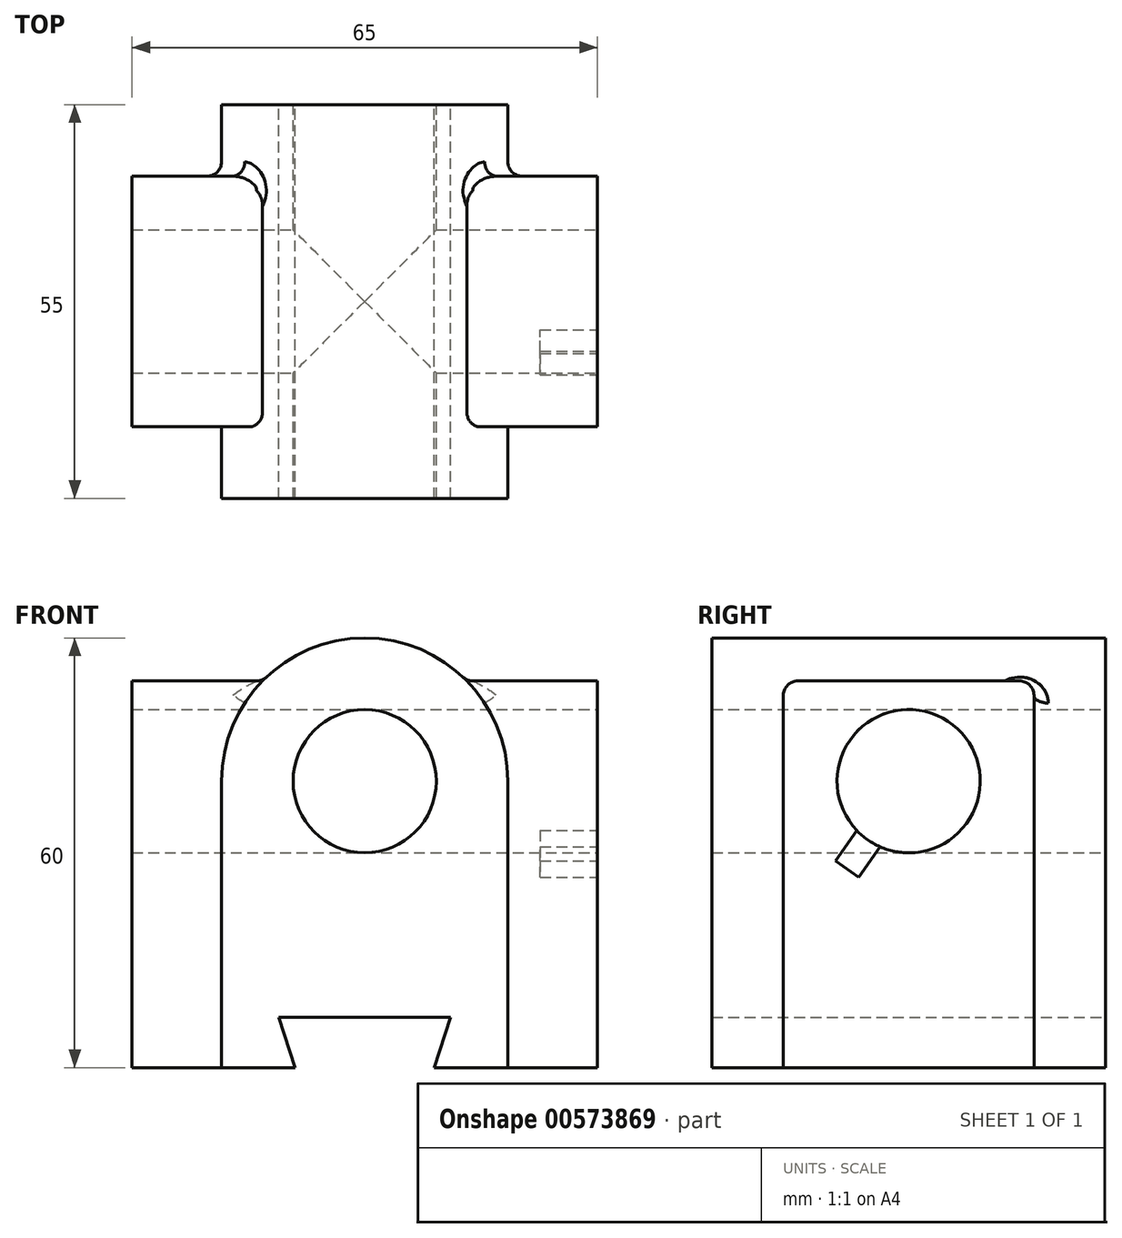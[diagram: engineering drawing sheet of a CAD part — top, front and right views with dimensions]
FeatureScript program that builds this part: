
annotation { "Feature Type Name" : "Feature", "Feature Type Description" : "" }
export const myFeature = defineFeature(function(context is Context, id is Id, definition is map)
    precondition{}
    {
        {
            var Q0;
            Q0=qCreatedBy(makeId("Front.planeOp"),FACE);
            var sketch = newSketch(context, id + "F0", { "sketchPlane" : qUnion([Q0])});
            skLineSegment(sketch, "E0.top", {"start": v(-20, -40) * mm, "end": v(-9.73, -40) * mm});
            skLineSegment(sketch, "E0.left", {"start": v(-20, 0) * mm, "end": v(-20, -40) * mm});
            skLineSegment(sketch, "E0.right", {"start": v(20, 0) * mm, "end": v(20, -40) * mm});
            skArc(sketch, "E1", {"start": v(20, 0) * mm, "mid": v(0, 20) * mm, "end": v(-20, 0) * mm});
            skCircle(sketch, "E2", {"center": v(0, 0) * mm, "radius": 10 * mm});
            skLineSegment(sketch, "E3", {"start": v(-12, -33) * mm, "end": v(-9.73, -40) * mm});
            skLineSegment(sketch, "E4", {"start": v(9.73, -40) * mm, "end": v(12, -33) * mm});
            skLineSegment(sketch, "E5", {"start": v(12, -33) * mm, "end": v(-12, -33) * mm});
            skLineSegment(sketch, "E6.trimOffspring", {"start": v(9.73, -40) * mm, "end": v(20, -40) * mm});
            skSolve(sketch);
        }
        {
            var Q0;
            Q0 = qSketchRegion(id + "F0", true);
            extrude(context, id + "F1", {"entities" : qUnion([Q0]), "depth" : 55 * mm, "offsetDistance" : 25 * mm});
        }
        {
            var Q0;
            Q0=makeQuery(id+"F1.opExtrude","SWEPT_FACE",FACE,{"disambiguationData":[OSD([sQuery(id+"F0.wireOp",EDGE,"E0.left")])]});
            var sketch = newSketch(context, id + "F2", { "sketchPlane" : qUnion([Q0])});
            skLineSegment(sketch, "E7.bottom", {"start": v(10, 14) * mm, "end": v(45, 14) * mm});
            skLineSegment(sketch, "E7.top", {"start": v(10, -40) * mm, "end": v(45, -40) * mm});
            skLineSegment(sketch, "E7.left", {"start": v(10, 14) * mm, "end": v(10, -40) * mm});
            skLineSegment(sketch, "E7.right", {"start": v(45, 14) * mm, "end": v(45, -40) * mm});
            skSolve(sketch);
        }
        {
            var Q0;
            {var subQ0=sQuery(id+"F2.wireOp",EDGE,"E7.bottom");Q0=makeQuery(id+"F2.imprint","IMPRINT",FACE,{"disambiguationData":[TD([[makeQuery(id+"F2.imprint","IMPRINT",EDGE,{"derivedFrom":subQ0}),-1.0]])]});}
            var Q1;
            {var subQ0=sQuery(id+"F2.wireOp",EDGE,"E7.top");Q1=makeQuery(id+"F2.imprint","IMPRINT",FACE,{"disambiguationData":[TD([[makeQuery(id+"F2.imprint","IMPRINT",EDGE,{"derivedFrom":subQ0}),-1.0]])]});}
            extrude(context, id + "F3", {"entities" : qUnion([Q0, Q1]), "operationType" : NewBodyOperationType.ADD, "depth" : 12.5 * mm, "offsetDistance" : 25 * mm});
        }
        {
            var Q0;
            Q0=makeQuery(id+"F1.opExtrude","SWEPT_FACE",FACE,{"disambiguationData":[OSD([sQuery(id+"F0.wireOp",EDGE,"E0.right")])]});
            var sketch = newSketch(context, id + "F4", { "sketchPlane" : qUnion([Q0])});
            skLineSegment(sketch, "E8.bottom", {"start": v(-45, 14) * mm, "end": v(-10, 14) * mm});
            skLineSegment(sketch, "E8.top", {"start": v(-45, -40) * mm, "end": v(-10, -40) * mm});
            skLineSegment(sketch, "E8.left", {"start": v(-45, 14) * mm, "end": v(-45, -40) * mm});
            skLineSegment(sketch, "E8.right", {"start": v(-10, 14) * mm, "end": v(-10, -40) * mm});
            skSolve(sketch);
        }
        {
            var Q0;
            {var subQ0=sQuery(id+"F4.wireOp",EDGE,"E8.top");Q0=makeQuery(id+"F4.imprint","IMPRINT",FACE,{"disambiguationData":[TD([[makeQuery(id+"F4.imprint","IMPRINT",EDGE,{"derivedFrom":subQ0}),1.0]])]});}
            var Q1;
            {var subQ0=sQuery(id+"F4.wireOp",EDGE,"E8.bottom");Q1=makeQuery(id+"F4.imprint","IMPRINT",FACE,{"disambiguationData":[TD([[makeQuery(id+"F4.imprint","IMPRINT",EDGE,{"derivedFrom":subQ0}),-1.0]])]});}
            extrude(context, id + "F5", {"entities" : qUnion([Q0, Q1]), "operationType" : NewBodyOperationType.ADD, "depth" : 12.5 * mm, "offsetDistance" : 25 * mm});
        }
        {
            var Q0;
            Q0=makeQuery(id+"F5.opExtrude","SWEPT_FACE",FACE,{"disambiguationData":[OSD([sQuery(id+"F4.wireOp",EDGE,"E8.left")])]});
            var sketch = newSketch(context, id + "F6", { "sketchPlane" : qUnion([Q0])});
            skLineSegment(sketch, "E9.0", {"start": v(20, 14) * mm, "end": v(20, 0) * mm});
            skLineSegment(sketch, "E10.0", {"start": v(-20, 14) * mm, "end": v(-20, 0) * mm});
            skLineSegment(sketch, "E11", {"start": v(20, 14) * mm, "end": v(14.28, 14) * mm});
            skLineSegment(sketch, "E12", {"start": v(-20, 14) * mm, "end": v(-14.28, 14) * mm});
            skArc(sketch, "E13.0", {"start": v(20, 0) * mm, "mid": v(0, 20) * mm, "end": v(-20, 0) * mm});
            skSolve(sketch);
        }
        {
            var Q0;
            {var subQ0=sQuery(id+"F6.wireOp",EDGE,"E10.0");Q0=makeQuery(id+"F6.imprint","IMPRINT",FACE,{"disambiguationData":[TD([[makeQuery(id+"F6.imprint","IMPRINT",EDGE,{"derivedFrom":subQ0}),1.0]])]});}
            var Q1;
            {var subQ0=sQuery(id+"F6.wireOp",EDGE,"E9.0");Q1=makeQuery(id+"F6.imprint","IMPRINT",FACE,{"disambiguationData":[TD([[makeQuery(id+"F6.imprint","IMPRINT",EDGE,{"derivedFrom":subQ0}),-1.0]])]});}
            extrude(context, id + "F7", {"entities" : qUnion([Q0, Q1]), "operationType" : NewBodyOperationType.ADD, "oppositeDirection" : true, "depth" : 35 * mm, "offsetDistance" : 25 * mm});
        }
        {
            var Q0;
            Q0=makeQuery(id+"F5.opExtrude","CAP_FACE",FACE,{"disambiguationData":[OSD([sQuery(id+"F4.wireOp",EDGE,"E8.bottom"),sQuery(id+"F4.wireOp",EDGE,"E8.top"),sQuery(id+"F4.wireOp",EDGE,"E8.left"),sQuery(id+"F4.wireOp",EDGE,"E8.right")])],"isStart":false});
            var sketch = newSketch(context, id + "F8", { "sketchPlane" : qUnion([Q0])});
            skCircle(sketch, "E14", {"center": v(-27.5, 0) * mm, "radius": 10 * mm});
            skSolve(sketch);
        }
        {
            var Q0;
            Q0=makeQuery(id+"F8.imprint","IMPRINT",FACE,{"disambiguationData":[TD([[makeQuery(id+"F8.imprint","IMPRINT",EDGE,{"derivedFrom":sQuery(id+"F8.wireOp",EDGE,"E14")}),1.0]])]});
            extrude(context, id + "F9", {"entities" : qUnion([Q0]), "operationType" : NewBodyOperationType.REMOVE, "oppositeDirection" : true, "depth" : 70 * mm, "offsetDistance" : 25 * mm});
        }
        {
            var Q0;
            Q0=makeQuery(id+"F7.boolean.opBoolean","MERGE",EDGE,{"derivedFrom":[makeQuery(id+"F3.opExtrude","SWEPT_EDGE",EDGE,{"disambiguationData":[OSD([sQuery(id+"F2.wireOp",EDGE,"E7.bottom"),sQuery(id+"F2.wireOp",EDGE,"E7.left")])]}),makeQuery(id+"F7.opExtrude","CAP_EDGE",EDGE,{"disambiguationData":[OSD([sQuery(id+"F6.wireOp",EDGE,"E12")])],"isStart":false})]});
            var Q1;
            Q1=makeQuery(id+"F7.boolean.opBoolean","MERGE",EDGE,{"derivedFrom":[makeQuery(id+"F3.opExtrude","SWEPT_EDGE",EDGE,{"disambiguationData":[OSD([sQuery(id+"F2.wireOp",EDGE,"E7.bottom"),sQuery(id+"F2.wireOp",EDGE,"E7.right")])]}),makeQuery(id+"F7.opExtrude","CAP_EDGE",EDGE,{"disambiguationData":[OSD([sQuery(id+"F6.wireOp",EDGE,"E12")])],"isStart":true})]});
            var Q2;
            Q2=makeQuery(id+"F7.boolean.opBoolean","MERGE",EDGE,{"derivedFrom":[makeQuery(id+"F5.opExtrude","SWEPT_EDGE",EDGE,{"disambiguationData":[OSD([sQuery(id+"F4.wireOp",EDGE,"E8.bottom"),sQuery(id+"F4.wireOp",EDGE,"E8.right")])]}),makeQuery(id+"F7.opExtrude","CAP_EDGE",EDGE,{"disambiguationData":[OSD([sQuery(id+"F6.wireOp",EDGE,"E11")])],"isStart":false})]});
            var Q3;
            Q3=makeQuery(id+"F7.boolean.opBoolean","MERGE",EDGE,{"derivedFrom":[makeQuery(id+"F5.opExtrude","SWEPT_EDGE",EDGE,{"disambiguationData":[OSD([sQuery(id+"F4.wireOp",EDGE,"E8.bottom"),sQuery(id+"F4.wireOp",EDGE,"E8.left")])]}),makeQuery(id+"F7.opExtrude","CAP_EDGE",EDGE,{"disambiguationData":[OSD([sQuery(id+"F6.wireOp",EDGE,"E11")])],"isStart":true})]});
            var Q4;
            {var subQ0=sQuery(id+"F4.wireOp",EDGE,"E8.right");Q4=makeQuery(id+"F5.boolean.opBoolean","SPLIT",EDGE,{"disambiguationData":[topologyDisambiguationEdgeConnected([makeQuery(id+"F1.opExtrude","SWEPT_FACE",FACE,{"disambiguationData":[OSD([sQuery(id+"F0.wireOp",EDGE,"E0.right")])]})])],"derivedFrom":makeQuery(id+"F5.opExtrude","CAP_EDGE",EDGE,{"disambiguationData":[OSD([subQ0])],"isStart":true})});}
            var Q5;
            {var subQ0=sQuery(id+"F2.wireOp",EDGE,"E7.left");Q5=makeQuery(id+"F3.boolean.opBoolean","SPLIT",EDGE,{"disambiguationData":[topologyDisambiguationEdgeConnected([makeQuery(id+"F1.opExtrude","SWEPT_FACE",FACE,{"disambiguationData":[OSD([sQuery(id+"F0.wireOp",EDGE,"E0.left")])]})])],"derivedFrom":makeQuery(id+"F3.opExtrude","CAP_EDGE",EDGE,{"disambiguationData":[OSD([subQ0])],"isStart":true})});}
            fillet(context, id + "F10", {"entities" : qUnion([Q0, Q1, Q2, Q3, Q4, Q5]), "radius" : 2 * mm, "tangentPropagation" : true, "allowEdgeOverflow" : false});
        }
        {
            var Q0;
            Q0=makeQuery(id+"F5.opExtrude","CAP_FACE",FACE,{"disambiguationData":[OSD([sQuery(id+"F4.wireOp",EDGE,"E8.bottom"),sQuery(id+"F4.wireOp",EDGE,"E8.top"),sQuery(id+"F4.wireOp",EDGE,"E8.left"),sQuery(id+"F4.wireOp",EDGE,"E8.right")])],"isStart":false});
            var sketch = newSketch(context, id + "F11", { "sketchPlane" : qUnion([Q0])});
            skLineSegment(sketch, "E15", {"start": v(-33.15, -4.59) * mm, "end": v(-37.74, -11.14) * mm});
            skLineSegment(sketch, "E16", {"start": v(-37.74, -11.14) * mm, "end": v(-34.47, -13.43) * mm});
            skLineSegment(sketch, "E17", {"start": v(-34.47, -13.43) * mm, "end": v(-29.88, -6.88) * mm});
            skLineSegment(sketch, "E18", {"start": v(-29.88, -6.88) * mm, "end": v(-33.15, -4.59) * mm});
            skPoint(sketch, "E19", {"position": v(-27.5, 0) * mm});
            skLineSegment(sketch, "E20", {"start": v(-5.9, 30.85) * mm, "end": v(-49.8, -31.86) * mm});
            skPoint(sketch, "E21", {"position": v(-33.24, -8.2) * mm});
            skSolve(sketch);
        }
        {
            var Q0;
            {var subQ0=sQuery(id+"F11.wireOp",EDGE,"E18");var subQ1=sQuery(id+"F11.wireOp",EDGE,"E17");var subQ2=makeQuery(id+"F11.imprint","INTERSECT",VERTEX,{"derivedFrom":[subQ1,subQ0]});Q0=makeQuery(id+"F11.imprint","IMPRINT",FACE,{"disambiguationData":[TD([[makeQuery(id+"F11.imprint","IMPRINT",EDGE,{"disambiguationData":[TD([[subQ2,1.0]])],"derivedFrom":subQ1}),1.0]])]});}
            var Q1;
            {var subQ0=sQuery(id+"F11.wireOp",EDGE,"E18");var subQ1=sQuery(id+"F11.wireOp",EDGE,"E15");var subQ2=makeQuery(id+"F11.imprint","INTERSECT",VERTEX,{"derivedFrom":[subQ1,subQ0]});Q1=makeQuery(id+"F11.imprint","IMPRINT",FACE,{"disambiguationData":[TD([[makeQuery(id+"F11.imprint","IMPRINT",EDGE,{"disambiguationData":[TD([[subQ2,-1.0]])],"derivedFrom":subQ1}),1.0]])]});}
            var Q2;
            {var subQ0=sQuery(id+"F11.wireOp",EDGE,"E16");var subQ1=sQuery(id+"F11.wireOp",EDGE,"E15");var subQ2=makeQuery(id+"F11.imprint","INTERSECT",VERTEX,{"derivedFrom":[subQ1,subQ0]});Q2=makeQuery(id+"F11.imprint","IMPRINT",FACE,{"disambiguationData":[TD([[makeQuery(id+"F11.imprint","IMPRINT",EDGE,{"disambiguationData":[TD([[subQ2,1.0]])],"derivedFrom":subQ1}),1.0]])]});}
            var Q3;
            {var subQ0=sQuery(id+"F11.wireOp",EDGE,"E17");var subQ1=sQuery(id+"F11.wireOp",EDGE,"E16");var subQ2=makeQuery(id+"F11.imprint","INTERSECT",VERTEX,{"derivedFrom":[subQ1,subQ0]});Q3=makeQuery(id+"F11.imprint","IMPRINT",FACE,{"disambiguationData":[TD([[makeQuery(id+"F11.imprint","IMPRINT",EDGE,{"disambiguationData":[TD([[subQ2,1.0]])],"derivedFrom":subQ1}),1.0]])]});}
            extrude(context, id + "F12", {"entities" : qUnion([Q0, Q1, Q2, Q3]), "operationType" : NewBodyOperationType.REMOVE, "oppositeDirection" : true, "depth" : 8 * mm, "offsetDistance" : 25 * mm});
        }
    });
